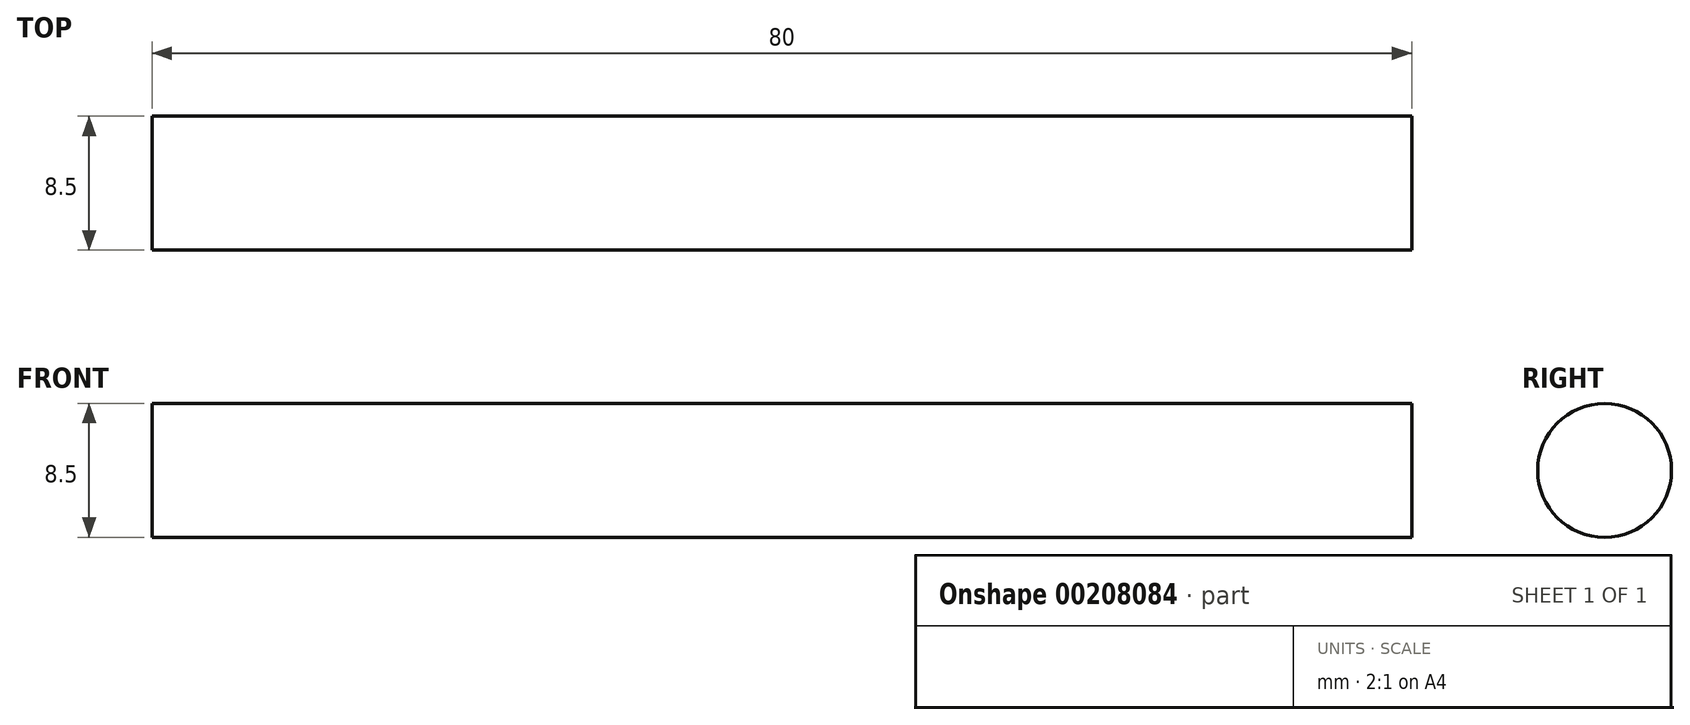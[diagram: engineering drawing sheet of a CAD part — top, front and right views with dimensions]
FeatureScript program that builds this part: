
annotation { "Feature Type Name" : "Feature", "Feature Type Description" : "" }
export const myFeature = defineFeature(function(context is Context, id is Id, definition is map)
    precondition{}
    {
        {
            var Q0;
            Q0=qCreatedBy(makeId("Top.planeOp"),FACE);
            var sketch = newSketch(context, id + "F0", { "sketchPlane" : qUnion([Q0])});
            skLineSegment(sketch, "E0.bottom", {"start": v(21, -21) * mm, "end": v(-21, -21) * mm, "construction": true});
            skLineSegment(sketch, "E0.top", {"start": v(21, 21) * mm, "end": v(-21, 21) * mm, "construction": true});
            skLineSegment(sketch, "E0.left", {"start": v(21, -21) * mm, "end": v(21, 21) * mm, "construction": true});
            skLineSegment(sketch, "E0.right", {"start": v(-21, -21) * mm, "end": v(-21, 21) * mm, "construction": true});
            skPoint(sketch, "E0.middle", {"position": v(0, 0) * mm});
            skLineSegment(sketch, "E1.bottom", {"start": v(15.5, -15.5) * mm, "end": v(-15.5, -15.5) * mm, "construction": true});
            skLineSegment(sketch, "E1.top", {"start": v(15.5, 15.5) * mm, "end": v(-15.5, 15.5) * mm, "construction": true});
            skLineSegment(sketch, "E1.left", {"start": v(15.5, -15.5) * mm, "end": v(15.5, 15.5) * mm, "construction": true});
            skLineSegment(sketch, "E1.right", {"start": v(-15.5, -15.5) * mm, "end": v(-15.5, 15.5) * mm, "construction": true});
            skCircle(sketch, "E2", {"center": v(0, 0) * mm, "radius": 15 * mm});
            skCircle(sketch, "E3", {"center": v(-15.5, -15.5) * mm, "radius": 2 * mm});
            skCircle(sketch, "E4", {"center": v(15.5, -15.5) * mm, "radius": 2 * mm});
            skCircle(sketch, "E5", {"center": v(15.5, 15.5) * mm, "radius": 2 * mm});
            skCircle(sketch, "E6", {"center": v(-15.5, 15.5) * mm, "radius": 2 * mm});
            skLineSegment(sketch, "E7.bottom", {"start": v(40, -19.5) * mm, "end": v(-40, -19.5) * mm, "construction": true});
            skLineSegment(sketch, "E7.top", {"start": v(40, 19.5) * mm, "end": v(-40, 19.5) * mm, "construction": true});
            skLineSegment(sketch, "E7.left", {"start": v(40, -19.5) * mm, "end": v(40, 19.5) * mm});
            skLineSegment(sketch, "E7.right", {"start": v(-40, -19.5) * mm, "end": v(-40, 19.5) * mm});
            skLineSegment(sketch, "E8", {"start": v(0, 0) * mm, "end": v(-28.5, 0) * mm, "construction": true});
            skLineSegment(sketch, "E9", {"start": v(0, 0) * mm, "end": v(0, 30.15) * mm, "construction": true});
            skPoint(sketch, "E9.endSnap0", {"position": v(0, 19.5) * mm});
            skLineSegment(sketch, "E10", {"start": v(-40, 19.5) * mm, "end": v(-40, 35) * mm});
            skLineSegment(sketch, "E11", {"start": v(-40, 35) * mm, "end": v(40, 35) * mm});
            skLineSegment(sketch, "E12", {"start": v(40, 35) * mm, "end": v(40, 19.5) * mm});
            skLineSegment(sketch, "E13.MirrorCS", {"start": v(-40, -35) * mm, "end": v(40, -35) * mm});
            skLineSegment(sketch, "E14.MirrorCS", {"start": v(-40, -19.5) * mm, "end": v(-40, -35) * mm});
            skLineSegment(sketch, "E15.MirrorCS", {"start": v(40, -35) * mm, "end": v(40, -19.5) * mm});
            skCircle(sketch, "E16", {"center": v(0, 0) * mm, "radius": 33.05 * mm, "construction": true});
            skCircle(sketch, "E17", {"center": v(33.05, 0) * mm, "radius": 3 * mm});
            skCircle(sketch, "E18.MirrorC", {"center": v(-33.05, 0) * mm, "radius": 3 * mm});
            skSolve(sketch);
        }
        {
            var Q0;
            Q0=makeQuery(id+"F0.imprint","IMPRINT",FACE,{"disambiguationData":[TD([[makeQuery(id+"F0.imprint","IMPRINT",EDGE,{"derivedFrom":sQuery(id+"F0.wireOp",EDGE,"E2")}),-1.0]])]});
            extrude(context, id + "F1", {"entities" : qUnion([Q0]), "depth" : 15 * mm, "offsetDistance" : 25 * mm});
        }
        {
            var Q0;
            Q0=makeQuery(id+"F1.opExtrude","SWEPT_FACE",FACE,{"disambiguationData":[OSD([sQuery(id+"F0.wireOp",EDGE,"E7.left"),sQuery(id+"F0.wireOp",EDGE,"E12"),sQuery(id+"F0.wireOp",EDGE,"E15.MirrorCS")])]});
            var sketch = newSketch(context, id + "F2", { "sketchPlane" : qUnion([Q0])});
            skLineSegment(sketch, "E19", {"start": v(0, 0) * mm, "end": v(0, 15) * mm, "construction": true});
            skCircle(sketch, "E20", {"center": v(26.15, 7.5) * mm, "radius": 4.25 * mm});
            skPoint(sketch, "E20.centerSnap0", {"position": v(35, 7.5) * mm});
            skCircle(sketch, "E21.MirrorC", {"center": v(-26.15, 7.5) * mm, "radius": 4.25 * mm});
            skSolve(sketch);
        }
        {
            var Q0;
            Q0=makeQuery(id+"F2.imprint","IMPRINT",FACE,{"disambiguationData":[TD([[makeQuery(id+"F2.imprint","IMPRINT",EDGE,{"derivedFrom":sQuery(id+"F2.wireOp",EDGE,"E21.MirrorC")}),-1.0]])]});
            var Q1;
            Q1=makeQuery(id+"F2.imprint","IMPRINT",FACE,{"disambiguationData":[TD([[makeQuery(id+"F2.imprint","IMPRINT",EDGE,{"derivedFrom":sQuery(id+"F2.wireOp",EDGE,"E20")}),1.0]])]});
            extrude(context, id + "F3", {"entities" : qUnion([Q0, Q1]), "operationType" : NewBodyOperationType.REMOVE, "endBound" : BoundingType.UP_TO_NEXT, "oppositeDirection" : true, "depth" : 25 * mm, "offsetDistance" : 25 * mm});
        }
    });
